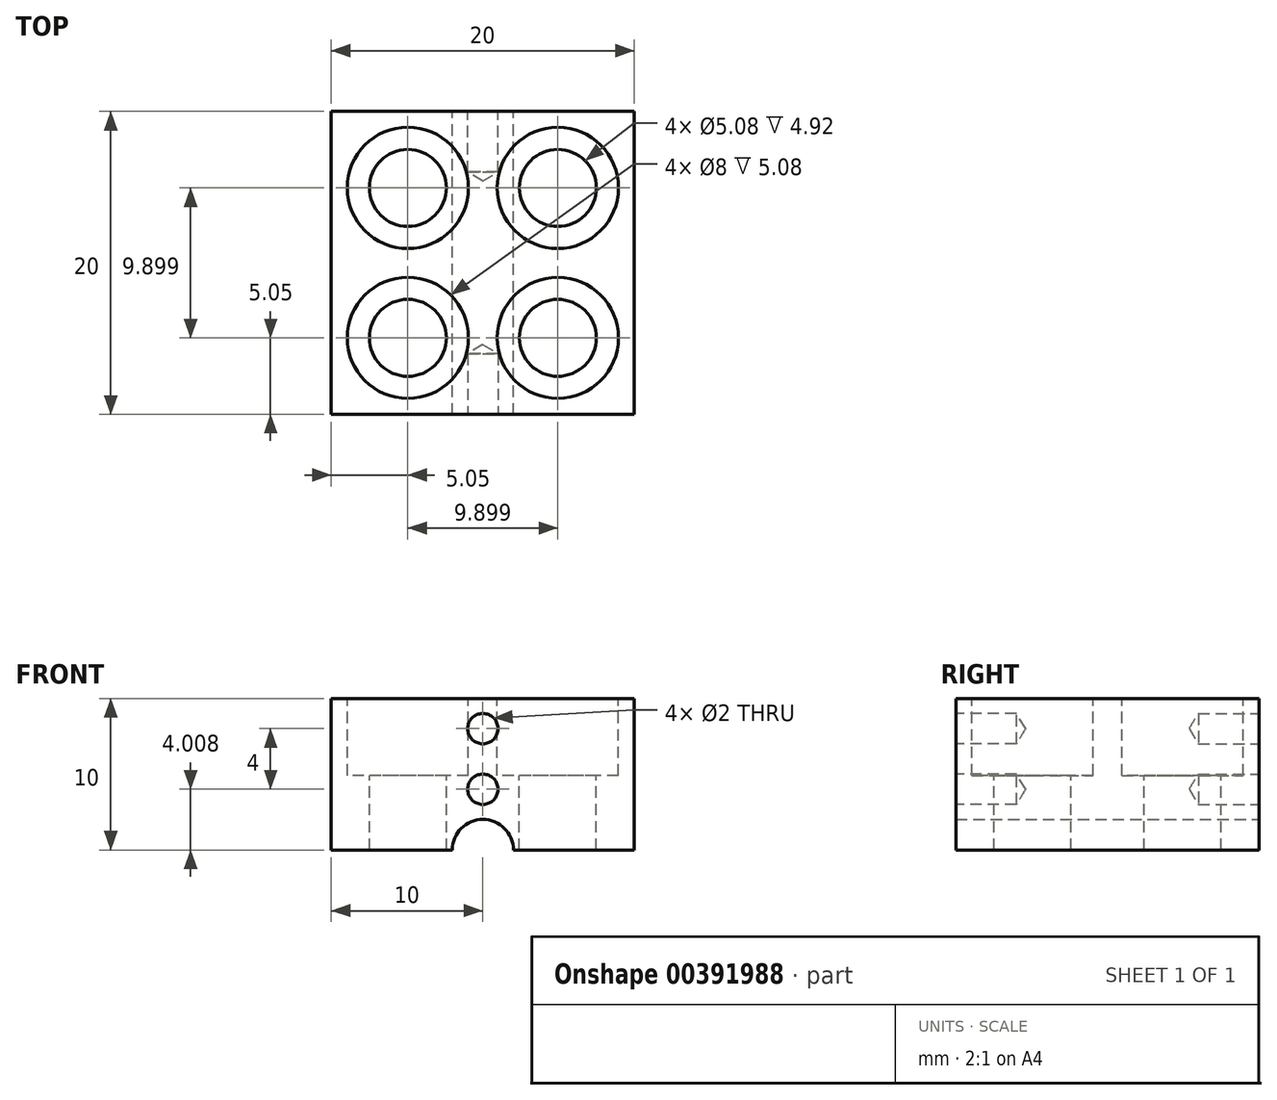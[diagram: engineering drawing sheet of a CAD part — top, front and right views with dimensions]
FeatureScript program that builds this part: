
annotation { "Feature Type Name" : "Feature", "Feature Type Description" : "" }
export const myFeature = defineFeature(function(context is Context, id is Id, definition is map)
    precondition{}
    {
        {
            var Q0;
            Q0=qCreatedBy(makeId("Top.planeOp"),FACE);
            var sketch = newSketch(context, id + "F0", { "sketchPlane" : qUnion([Q0])});
            skLineSegment(sketch, "E0.bottom", {"start": v(10, 10) * mm, "end": v(-10, 10) * mm});
            skLineSegment(sketch, "E0.top", {"start": v(10, -10) * mm, "end": v(-10, -10) * mm});
            skLineSegment(sketch, "E0.left", {"start": v(10, 10) * mm, "end": v(10, -10) * mm});
            skLineSegment(sketch, "E0.right", {"start": v(-10, 10) * mm, "end": v(-10, -10) * mm});
            skPoint(sketch, "E0.middle", {"position": v(0, 0) * mm});
            skSolve(sketch);
        }
        {
            var Q0;
            Q0=makeQuery(id+"F0.imprint","IMPRINT",FACE,{"disambiguationData":[TD([[makeQuery(id+"F0.imprint","IMPRINT",EDGE,{"derivedFrom":sQuery(id+"F0.wireOp",EDGE,"E0.bottom")}),1.0]])]});
            extrude(context, id + "F1", {"entities" : qUnion([Q0]), "depth" : 10 * mm});
        }
        {
            var Q0;
            Q0=qCreatedBy(makeId("Front.planeOp"),FACE);
            var sketch = newSketch(context, id + "F2", { "sketchPlane" : qUnion([Q0])});
            skCircle(sketch, "E1", {"center": v(0, 0) * mm, "radius": 2.02 * mm});
            skSolve(sketch);
        }
        {
            var Q0;
            Q0 = qSketchRegion(id + "F2", true);
            extrude(context, id + "F3", {"entities" : qUnion([Q0]), "operationType" : NewBodyOperationType.REMOVE, "depth" : 25 * mm, "hasSecondDirection" : true, "secondDirectionOppositeDirection" : true, "secondDirectionDepth" : 25 * mm});
        }
        {
            var Q0;
            Q0=makeQuery(id+"F1.opExtrude","CAP_FACE",FACE,{"disambiguationData":[OSD([sQuery(id+"F0.wireOp",EDGE,"E0.bottom"),sQuery(id+"F0.wireOp",EDGE,"E0.top"),sQuery(id+"F0.wireOp",EDGE,"E0.left"),sQuery(id+"F0.wireOp",EDGE,"E0.right")])],"isStart":false});
            var sketch = newSketch(context, id + "F4", { "sketchPlane" : qUnion([Q0])});
            skLineSegment(sketch, "E2", {"start": v(-10, -10) * mm, "end": v(10, 10) * mm});
            skLineSegment(sketch, "E3", {"start": v(-10, 10) * mm, "end": v(10, -10) * mm});
            skCircle(sketch, "E4", {"center": v(0, 0) * mm, "radius": 7 * mm});
            skPoint(sketch, "E5", {"position": v(-4.95, 4.95) * mm});
            skPoint(sketch, "E6", {"position": v(4.95, 4.95) * mm});
            skPoint(sketch, "E7", {"position": v(-4.95, -4.95) * mm});
            skPoint(sketch, "E8", {"position": v(4.95, -4.95) * mm});
            skSolve(sketch);
        }
        {
            var Q0;
            Q0=sQuery(id+"F4.wireOp",VERTEX,"E5");
            var Q1;
            Q1=sQuery(id+"F4.wireOp",VERTEX,"E7");
            var Q2;
            Q2=sQuery(id+"F4.wireOp",VERTEX,"E8");
            var Q3;
            Q3=sQuery(id+"F4.wireOp",VERTEX,"E6");
            var Q4;
            Q4=makeQuery(id+"F1.opExtrude","SWEPT_BODY",BODY,{"disambiguationData":[OSD([sQuery(id+"F0.wireOp",EDGE,"E0.bottom"),sQuery(id+"F0.wireOp",EDGE,"E0.top"),sQuery(id+"F0.wireOp",EDGE,"E0.left"),sQuery(id+"F0.wireOp",EDGE,"E0.right")])]});
            hole(context, id + "F5", {"style" : HoleStyle.C_BORE, "endStyle" : HoleEndStyle.THROUGH, "holeDiameter" : 5.08 * mm, "cBoreDiameter" : 8 * mm, "cBoreDepth" : 5.08 * mm, "isTappedThrough" : true, "tappedDepth" : 12 * mm, "tapClearance" : 3, "locations" : qUnion([Q0, Q1, Q2, Q3]), "scope" : qUnion([Q4])});
        }
        {
            var Q0;
            Q0=makeQuery(id+"F1.opExtrude","SWEPT_FACE",FACE,{"disambiguationData":[OSD([sQuery(id+"F0.wireOp",EDGE,"E0.top")])]});
            var sketch = newSketch(context, id + "F6", { "sketchPlane" : qUnion([Q0])});
            skLineSegment(sketch, "E9", {"start": v(-10, 2.02) * mm, "end": v(10, 2.02) * mm});
            skLineSegment(sketch, "E10", {"start": v(-10, 2.02) * mm, "end": v(10, 10) * mm});
            skLineSegment(sketch, "E11", {"start": v(-10, 10) * mm, "end": v(10, 2.02) * mm});
            skCircle(sketch, "E12", {"center": v(0, 6) * mm, "radius": 2 * mm});
            skLineSegment(sketch, "E13", {"start": v(0, 10) * mm, "end": v(0, 2.02) * mm});
            skPoint(sketch, "E14", {"position": v(0, 8) * mm});
            skPoint(sketch, "E15", {"position": v(0, 4) * mm});
            skSolve(sketch);
        }
        {
            var Q0;
            Q0=sQuery(id+"F6.wireOp",VERTEX,"E14");
            var Q1;
            Q1=sQuery(id+"F6.wireOp",VERTEX,"E15");
            var Q2;
            Q2=makeQuery(id+"F1.opExtrude","SWEPT_BODY",BODY,{"disambiguationData":[OSD([sQuery(id+"F0.wireOp",EDGE,"E0.bottom"),sQuery(id+"F0.wireOp",EDGE,"E0.top"),sQuery(id+"F0.wireOp",EDGE,"E0.left"),sQuery(id+"F0.wireOp",EDGE,"E0.right")])]});
            hole(context, id + "F7", {"style" : HoleStyle.SIMPLE, "endStyle" : HoleEndStyle.BLIND, "holeDiameter" : 2 * mm, "holeDepth" : 4 * mm, "isTappedThrough" : true, "tappedDepth" : 12 * mm, "tapClearance" : 3, "locations" : qUnion([Q0, Q1]), "scope" : qUnion([Q2])});
        }
        {
            var Q0;
            Q0=makeQuery(id+"F1.opExtrude","SWEPT_FACE",FACE,{"disambiguationData":[OSD([sQuery(id+"F0.wireOp",EDGE,"E0.bottom")])]});
            var sketch = newSketch(context, id + "F8", { "sketchPlane" : qUnion([Q0])});
            skLineSegment(sketch, "E16", {"start": v(-10, 2.02) * mm, "end": v(10, 2.02) * mm});
            skLineSegment(sketch, "E17", {"start": v(-10, 10) * mm, "end": v(10, 2.02) * mm});
            skLineSegment(sketch, "E18", {"start": v(10, 10) * mm, "end": v(-10, 2.02) * mm});
            skCircle(sketch, "E19", {"center": v(0, 6) * mm, "radius": 2 * mm});
            skLineSegment(sketch, "E20", {"start": v(0, 2.02) * mm, "end": v(0, 10) * mm});
            skPoint(sketch, "E21", {"position": v(0, 8) * mm});
            skPoint(sketch, "E22", {"position": v(0, 4) * mm});
            skSolve(sketch);
        }
        {
            var Q0;
            Q0=sQuery(id+"F8.wireOp",VERTEX,"E22");
            var Q1;
            Q1=sQuery(id+"F8.wireOp",VERTEX,"E21");
            var Q2;
            Q2=makeQuery(id+"F1.opExtrude","SWEPT_BODY",BODY,{"disambiguationData":[OSD([sQuery(id+"F0.wireOp",EDGE,"E0.bottom"),sQuery(id+"F0.wireOp",EDGE,"E0.top"),sQuery(id+"F0.wireOp",EDGE,"E0.left"),sQuery(id+"F0.wireOp",EDGE,"E0.right")])]});
            hole(context, id + "F9", {"style" : HoleStyle.SIMPLE, "endStyle" : HoleEndStyle.BLIND, "holeDiameter" : 2 * mm, "holeDepth" : 4 * mm, "isTappedThrough" : true, "tappedDepth" : 12 * mm, "tapClearance" : 3, "locations" : qUnion([Q0, Q1]), "scope" : qUnion([Q2])});
        }
    });
